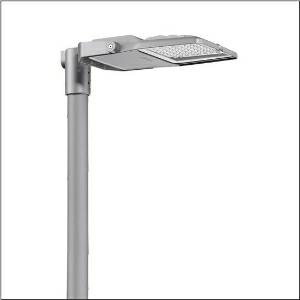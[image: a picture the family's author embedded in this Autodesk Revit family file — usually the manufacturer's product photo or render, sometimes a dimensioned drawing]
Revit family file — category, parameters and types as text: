
# Revit family: floodlight_fl_21_mini___pl43_5xa7772d4a3a_bc30
name_source: partatom
category: Lighting Fixtures
units: mm (PartAtom-declared; Revit-internal decimal feet)

## family parameters
Cut with Voids When Loaded = No
Host = Face
Light Source = No
Part Type = Normal
Room Calculation Point = No
Round Connector Dimension = Use Diameter
Shared = No

## types (1)
- --- (1 x LED, 19090 lm, 143 W, 4000K)
    Apparent Load = 143 VA
    CIE Flux Codes = 27 78 99 100 100
    Color Rendering = 70
    Color Temperature = 4000K
    Default Elevation = 1800 mm
    Description = Floodlight FL 21 mini, floodlight, primary light control with lens, of PMMA, primary optical cover: protective disc, of toughened safety glass, transparent, light distribution: PL43, light emission: direct distribution, installation type: surface-mounted, LED, High Power LED, rated luminous flux: 19.090lm, luminous efficacy: 133lm/W, light colour: 740, colour temperature: 4000K, control gear: ECG iQ, control: Auto-Match, Temp-Guard, Night-Set, Smart-Wire, Desk-Remote (wireless, voltage-free reading and setting of iQ features in the workshop via application-optimized NFC function/RFID function), optimised constant luminous flux control (CLO 2.0), Light-Fading, Lumen-Switch, with terminal, 6-pole, mains connection: 220..240V, AC, 50/60Hz, start of lifetime: 143W, end of lifetime: 152W, reduction: 61W, luminaire housing, of diecast aluminium, powder-coated, Siteco® metallic grey (DB 702S), corrosivity category C5 according to DIN EN ISO 12944, mast bracket, of steel, galvanised, powder-coated, protection rating (complete): IP66, insulation class (complete): insulation class II (safety insulation), certification: CE, ENEC, VDE, protection symbol: D, impact resistance: IK08, permissible operating ambient temperature: -40..+40°C, permissible operating ambient temperature for outdoor applications: -40..+50°C, standard: DIN EN 12944, packaging unit: 1 piece

Light Distribution: PL43
    Height = 70 mm
    Lamp = 1 x LED
    Lamp Light Flux = 19090 lm
    Lamp Power = 143 W
    Lamp count = 1
    Length = 485 mm
    Luminous efficacy = 133 lm/W
    Manufacturer = Siteco
    ModVariant = No
    Model = 5XA7772D4A3A
    Number of Poles = 1
    OnlyDefault = Yes
    Power Factor = 1
    Product Name = Floodlight FL 21 mini | PL43
    Product group = floodlight | pylon top
    ProductGroupID = 6101
    Protection Class = Protection class II
    Protection Degree = IP 66
    RLX_Detail_Level = 1
    RlxData = <blob elided: 101409 chars, md5=899a524b>
    Socket = socket
    Standby Power = 0 W
    System Light Flux = 19090 lm
    System Power = 143 W
    Type Comments = factory setting: luminous flux: 100 % | dim-lin: 254 | 730 mA
    Type Image = l_1007125.jpg
    URL = http://relux.com
    VarID = @adj_072661
    Voltage = 0 V
    Weight = 0.00 kg
    Width = 337 mm

## geometry (parser evidence)
native form markers: Blend x4, Sweep x12
no freeform markers — native parametric forms only
